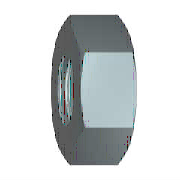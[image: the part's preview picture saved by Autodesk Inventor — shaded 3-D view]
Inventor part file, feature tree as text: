
AUTODESK INVENTOR PART (.ipt)
format: ipt  version: 2025 (Build 290162000, 162)  size: 168,960 bytes
history: native  units: mm (DEFAULTED — no unit token found)
features: extrude x1, chamfer x1, hole x1, other x1, plane x1
ambient origin geometry x7: Origin, YZ Plane, XZ Plane, X Axis, Y Axis, Z Axis, Center Point
bodies: Solid1 (feature_tree)
feature tree (5):
  extrude  "轴承体"  Depth=18.475209mm
  chamfer  "倒角1"  Distance=8.4mm
  hole  "螺纹"  [1 undecoded]
  other  "Work Axis1"
  plane  "Work Plane1"
note: 1 required parameter value undecoded (feature->parameter linkage not recoverable at this tier; creation-order binding heuristic only, values carry confidence <= 0.55)
